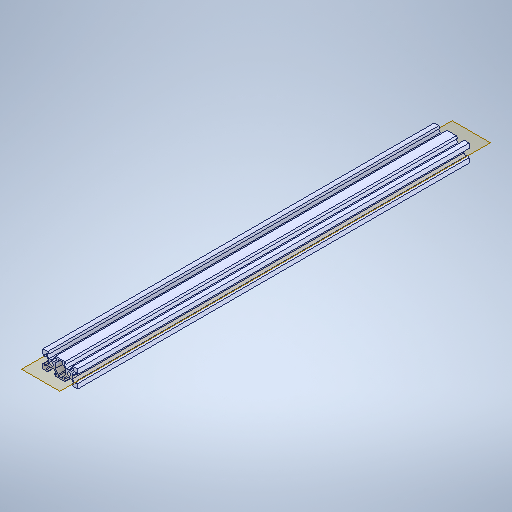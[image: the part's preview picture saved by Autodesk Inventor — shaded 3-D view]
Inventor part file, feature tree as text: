
AUTODESK INVENTOR PART (.ipt)
format: ipt  version: 2025.2 (Build 292293000, 293)  size: 359,424 bytes
history: native  units: in
note: dims shown in document units (in); Inventor stores cm internally (conversion verified against a paired STEP export)
features: extrude x1, sketch x1, other x1
ambient origin geometry x8: Origin, YZ Plane, XZ Plane, XY Plane, X Axis, Y Axis, Z Axis, Center Point
bodies: Solid1 (feature_tree)
feature tree (3):
  extrude  "Extrusion1"  [1 undecoded]
  sketch  "Sketch1"  dims[d0=1.9685in d1=0.0in]
  other  "Boss-Extrude1"
note: 1 required parameter value undecoded (feature->parameter linkage not recoverable at this tier; creation-order binding heuristic only, values carry confidence <= 0.55)
